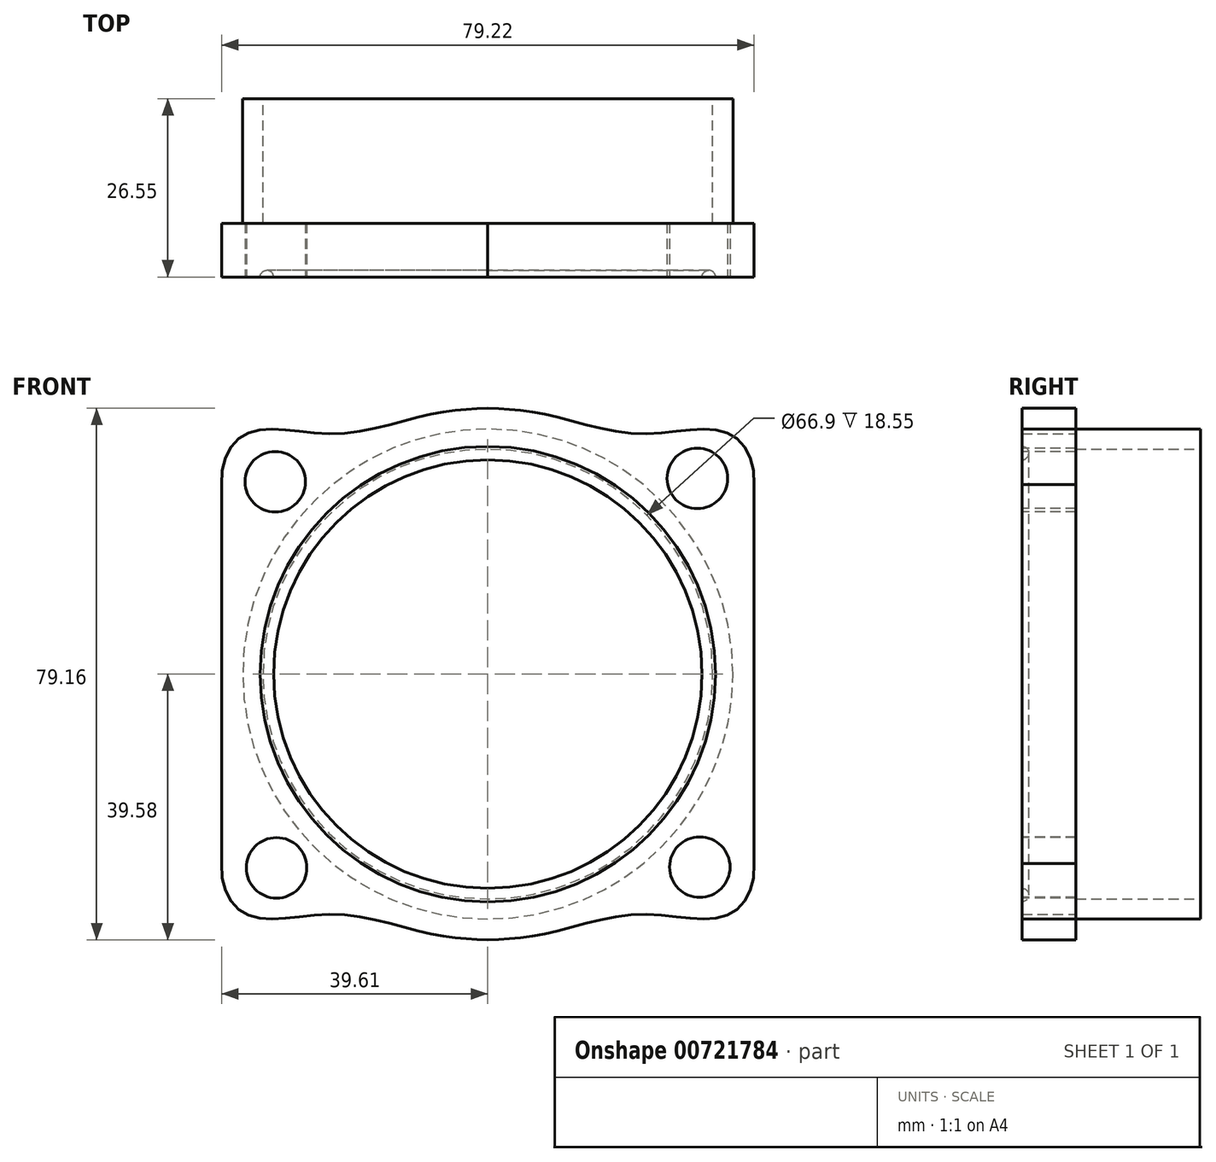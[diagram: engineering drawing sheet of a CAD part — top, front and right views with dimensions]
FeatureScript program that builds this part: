
annotation { "Feature Type Name" : "Feature", "Feature Type Description" : "" }
export const myFeature = defineFeature(function(context is Context, id is Id, definition is map)
    precondition{}
    {
        {
            var Q0;
            Q0=qCreatedBy(makeId("Front.planeOp"),FACE);
            var sketch = newSketch(context, id + "F0", { "sketchPlane" : qUnion([Q0])});
            skCircle(sketch, "E0", {"center": v(0, 0) * mm, "radius": 39.58 * mm, "construction": true});
            skLineSegment(sketch, "E1", {"start": v(-39.58, 0) * mm, "end": v(-39.58, 28.18) * mm});
            skPoint(sketch, "E2", {"position": v(-39.58, 0) * mm});
            skLineSegment(sketch, "E3", {"start": v(0, 0) * mm, "end": v(-45.8, 0) * mm, "construction": true});
            skPoint(sketch, "E4", {"position": v(0, 39.58) * mm});
            skPoint(sketch, "E5", {"position": v(-35.34, 36) * mm});
            skPoint(sketch, "E6", {"position": v(-23, 35.75) * mm});
            skFitSpline(sketch, "E7", {"points": [v(-39.58, 28.18) * mm, v(-35.34, 36) * mm, v(-23, 35.75) * mm, v(-8.68, 38.61) * mm, v(0, 39.57) * mm], "startDerivative": vector(-3.87, 52.15) * mm, "endDerivative": vector(36.88, 1.8) * mm});
            skFitSpline(sketch, "E8.MirrorCS", {"points": [v(39.58, 28.18) * mm, v(35.34, 36) * mm, v(23, 35.75) * mm, v(8.68, 38.61) * mm, v(0, 39.57) * mm], "startDerivative": vector(3.87, 52.15) * mm, "endDerivative": vector(-36.88, 1.8) * mm});
            skLineSegment(sketch, "E9.MirrorCS", {"start": v(39.58, 0) * mm, "end": v(39.58, 28.18) * mm});
            skLineSegment(sketch, "E10.MirrorCS", {"start": v(39.58, 0) * mm, "end": v(39.58, -28.18) * mm});
            skLineSegment(sketch, "E11.MirrorCS", {"start": v(-39.58, 0) * mm, "end": v(-39.58, -28.18) * mm});
            skFitSpline(sketch, "E12.MirrorCS", {"points": [v(39.58, -28.18) * mm, v(35.34, -36) * mm, v(23, -35.75) * mm, v(8.68, -38.61) * mm, v(0, -39.58) * mm], "startDerivative": vector(3.87, -52.15) * mm, "endDerivative": vector(-36.88, -1.8) * mm});
            skFitSpline(sketch, "E13.MirrorCS", {"points": [v(-39.58, -28.18) * mm, v(-35.34, -36) * mm, v(-23, -35.75) * mm, v(-8.68, -38.61) * mm, v(0, -39.58) * mm], "startDerivative": vector(-3.87, -52.15) * mm, "endDerivative": vector(36.88, -1.8) * mm});
            skSolve(sketch);
        }
        {
            var Q0;
            Q0 = qSketchRegion(id + "F0", true);
            extrude(context, id + "F1", {"entities" : qUnion([Q0]), "depth" : 8 * mm, "offsetDistance" : 25 * mm});
        }
        {
            var Q0;
            Q0=makeQuery(id+"F1.opExtrude","CAP_FACE",FACE,{"disambiguationData":[OSD([sQuery(id+"F0.wireOp",EDGE,"E1"),sQuery(id+"F0.wireOp",EDGE,"E7"),sQuery(id+"F0.wireOp",EDGE,"E8.MirrorCS"),sQuery(id+"F0.wireOp",EDGE,"E9.MirrorCS"),sQuery(id+"F0.wireOp",EDGE,"E10.MirrorCS"),sQuery(id+"F0.wireOp",EDGE,"E11.MirrorCS"),sQuery(id+"F0.wireOp",EDGE,"E12.MirrorCS"),sQuery(id+"F0.wireOp",EDGE,"E13.MirrorCS")])],"isStart":false});
            var sketch = newSketch(context, id + "F2", { "sketchPlane" : qUnion([Q0])});
            skCircle(sketch, "E14", {"center": v(-31.63, 28.62) * mm, "radius": 4.5 * mm});
            skCircle(sketch, "E15", {"center": v(31.17, 29.12) * mm, "radius": 4.5 * mm});
            skCircle(sketch, "E16", {"center": v(31.53, -28.72) * mm, "radius": 4.5 * mm});
            skCircle(sketch, "E17", {"center": v(-31.43, -28.83) * mm, "radius": 4.5 * mm});
            skSolve(sketch);
        }
        {
            var Q0;
            Q0=makeQuery(id+"F2.imprint","IMPRINT",FACE,{"disambiguationData":[TD([[makeQuery(id+"F2.imprint","IMPRINT",EDGE,{"derivedFrom":sQuery(id+"F2.wireOp",EDGE,"E14")}),1.0]])]});
            var Q1;
            Q1=makeQuery(id+"F2.imprint","IMPRINT",FACE,{"disambiguationData":[TD([[makeQuery(id+"F2.imprint","IMPRINT",EDGE,{"derivedFrom":sQuery(id+"F2.wireOp",EDGE,"E17")}),1.0]])]});
            var Q2;
            Q2=makeQuery(id+"F2.imprint","IMPRINT",FACE,{"disambiguationData":[TD([[makeQuery(id+"F2.imprint","IMPRINT",EDGE,{"derivedFrom":sQuery(id+"F2.wireOp",EDGE,"E16")}),1.0]])]});
            var Q3;
            Q3=makeQuery(id+"F2.imprint","IMPRINT",FACE,{"disambiguationData":[TD([[makeQuery(id+"F2.imprint","IMPRINT",EDGE,{"derivedFrom":sQuery(id+"F2.wireOp",EDGE,"E15")}),1.0]])]});
            extrude(context, id + "F3", {"entities" : qUnion([Q0, Q1, Q2, Q3]), "operationType" : NewBodyOperationType.REMOVE, "endBound" : BoundingType.UP_TO_NEXT, "oppositeDirection" : true, "depth" : 25 * mm, "offsetDistance" : 25 * mm});
        }
        {
            var Q0;
            Q0=makeQuery(id+"F1.opExtrude","CAP_FACE",FACE,{"disambiguationData":[OSD([sQuery(id+"F0.wireOp",EDGE,"E1"),sQuery(id+"F0.wireOp",EDGE,"E7"),sQuery(id+"F0.wireOp",EDGE,"E8.MirrorCS"),sQuery(id+"F0.wireOp",EDGE,"E9.MirrorCS"),sQuery(id+"F0.wireOp",EDGE,"E10.MirrorCS"),sQuery(id+"F0.wireOp",EDGE,"E11.MirrorCS"),sQuery(id+"F0.wireOp",EDGE,"E12.MirrorCS"),sQuery(id+"F0.wireOp",EDGE,"E13.MirrorCS")])],"isStart":true});
            var sketch = newSketch(context, id + "F4", { "sketchPlane" : qUnion([Q0])});
            skCircle(sketch, "E18", {"center": v(0, 0) * mm, "radius": 34.95 * mm});
            skSolve(sketch);
        }
        {
            var Q0;
            Q0=makeQuery(id+"F1.opExtrude","CAP_FACE",FACE,{"disambiguationData":[OSD([sQuery(id+"F0.wireOp",EDGE,"E1"),sQuery(id+"F0.wireOp",EDGE,"E7"),sQuery(id+"F0.wireOp",EDGE,"E8.MirrorCS"),sQuery(id+"F0.wireOp",EDGE,"E9.MirrorCS"),sQuery(id+"F0.wireOp",EDGE,"E10.MirrorCS"),sQuery(id+"F0.wireOp",EDGE,"E11.MirrorCS"),sQuery(id+"F0.wireOp",EDGE,"E12.MirrorCS"),sQuery(id+"F0.wireOp",EDGE,"E13.MirrorCS")])],"isStart":false});
            var sketch = newSketch(context, id + "F5", { "sketchPlane" : qUnion([Q0])});
            skCircle(sketch, "E19", {"center": v(0, 0) * mm, "radius": 32.88 * mm});
            skPoint(sketch, "E20", {"position": v(32.88, 0) * mm});
            skSolve(sketch);
        }
        {
            var Q0;
            Q0=qCreatedBy(makeId("Top.planeOp"),FACE);
            var sketch = newSketch(context, id + "F6", { "sketchPlane" : qUnion([Q0])});
            skCircle(sketch, "E21", {"center": v(32.88, -8) * mm, "radius": 1 * mm});
            skSolve(sketch);
        }
        {
            var Q0;
            Q0=makeQuery(id+"F6.imprint","IMPRINT",FACE,{"disambiguationData":[TD([[makeQuery(id+"F6.imprint","IMPRINT",EDGE,{"derivedFrom":sQuery(id+"F6.wireOp",EDGE,"E21")}),1.0]])]});
            var Q1;
            Q1=sQuery(id+"F5.wireOp",EDGE,"E19");
            sweep(context, id + "F7", {"operationType" : NewBodyOperationType.REMOVE, "profiles" : qUnion([Q0]), "path" : qUnion([Q1])});
        }
        {
            var Q0;
            Q0=qCreatedBy(makeId("Top.planeOp"),FACE);
            var sketch = newSketch(context, id + "F8", { "sketchPlane" : qUnion([Q0])});
            skLineSegment(sketch, "E22.bottom", {"start": v(33.45, 0) * mm, "end": v(36.45, 0) * mm});
            skLineSegment(sketch, "E22.top", {"start": v(33.45, 18.55) * mm, "end": v(36.45, 18.55) * mm});
            skLineSegment(sketch, "E22.left", {"start": v(33.45, 0) * mm, "end": v(33.45, 18.55) * mm});
            skLineSegment(sketch, "E22.right", {"start": v(36.45, 0) * mm, "end": v(36.45, 18.55) * mm});
            skPoint(sketch, "E23", {"position": v(34.95, 0) * mm});
            skSolve(sketch);
        }
        {
            var Q0;
            Q0=makeQuery(id+"F8.imprint","IMPRINT",FACE,{"disambiguationData":[TD([[makeQuery(id+"F8.imprint","IMPRINT",EDGE,{"derivedFrom":sQuery(id+"F8.wireOp",EDGE,"E22.bottom")}),1.0]])]});
            var Q1;
            Q1=sQuery(id+"F4.wireOp",EDGE,"E18");
            sweep(context, id + "F9", {"operationType" : NewBodyOperationType.ADD, "profiles" : qUnion([Q0]), "path" : qUnion([Q1])});
        }
    });
